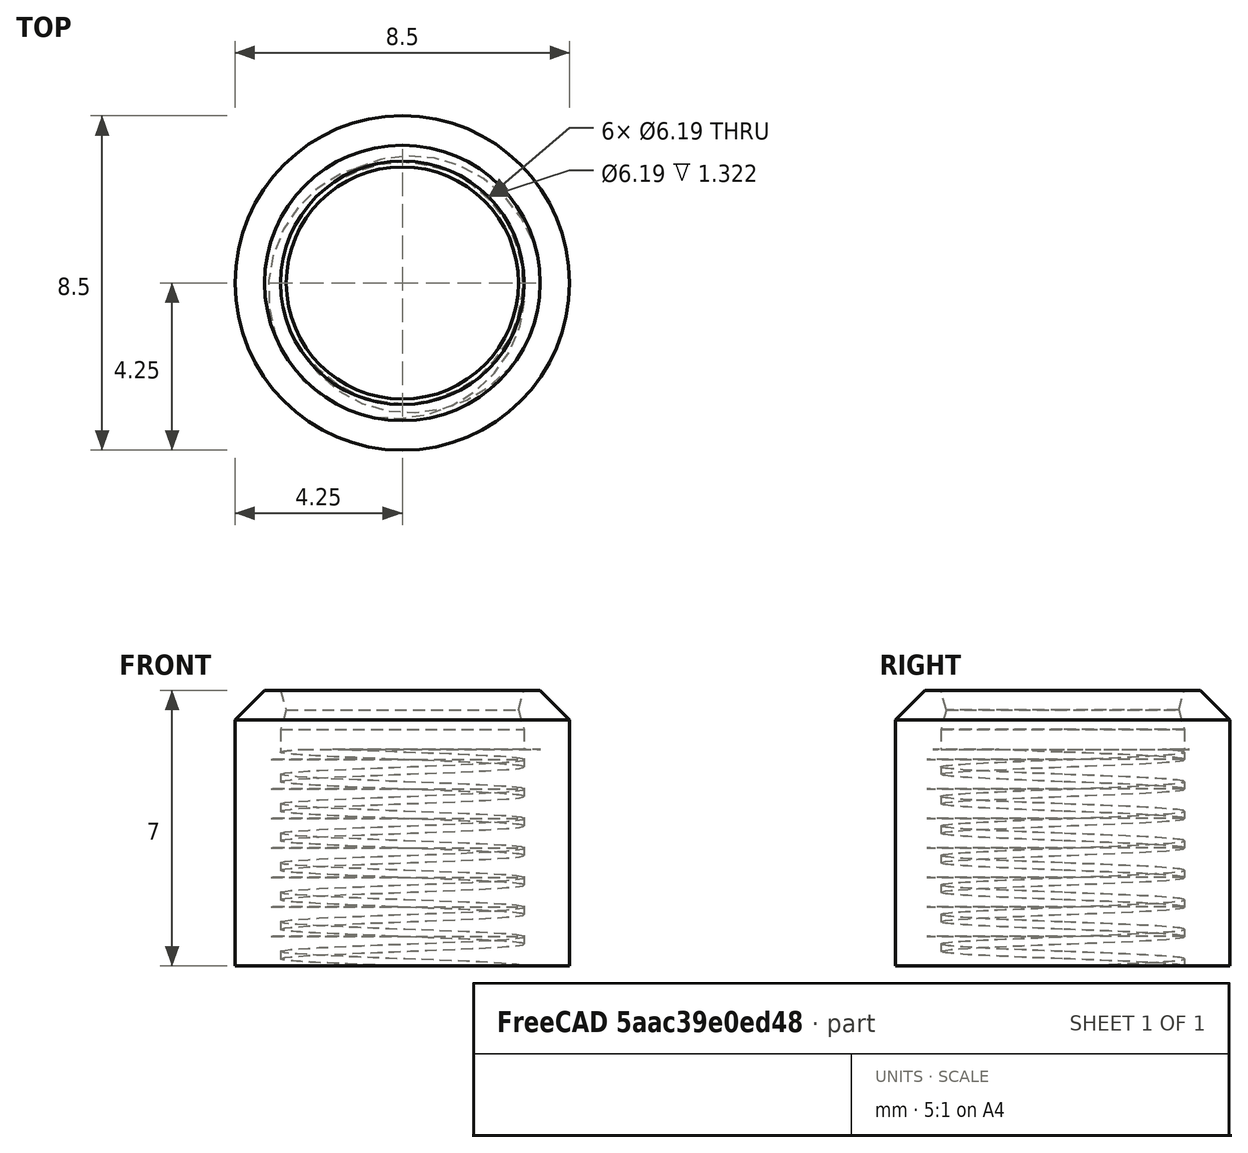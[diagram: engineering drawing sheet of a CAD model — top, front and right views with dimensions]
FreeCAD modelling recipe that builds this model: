
FCSTD DOCUMENT  (FreeCAD 0.21R33668 +26 (Git))
Label: PLASTIC-BUSHING-POT-TEK2
License: All rights reserved
LicenseURL: http://en.wikipedia.org/wiki/All_rights_reserved
objects: TechDraw::DrawViewDimension×9, Sketcher::SketchObject×2, TechDraw::DrawViewBalloon×2, TechDraw::DrawViewAnnotation×2, PartDesign::Revolution×1, TechDraw::DrawSVGTemplate×1, Part::Part2DObjectPython×1, Part::Helix×1, PartDesign::SubtractivePipe×1, PartDesign::Body×1, TechDraw::DrawViewPart×1, TechDraw::DrawComplexSection×1, TechDraw::DrawViewImage×1, TechDraw::DrawPage×1
note: 25 computed .brp shape members not serialized (recipe doc carries the construction recipe); baked Part::Feature solids carry a one-line shape summary decoded from their .brp

FEATURE [Sketcher::SketchObject] Sketch
  FullyConstrained = true
  MapMode = 5
  Placement = pos=(0,0,0) rot=(1,0,0;1.5708rad)
  Support = -> [XZ_Plane]
  sketch-geometry (7):
    g0: LineSegment StartX=-3.095 StartY=6 StartZ=0 EndX=-3.095 EndY=0 EndZ=0
    g1: LineSegment StartX=-3.095 StartY=7 StartZ=0 EndX=-3.5 EndY=7 EndZ=0
    g2: LineSegment StartX=-3.5 StartY=7 StartZ=0 EndX=-4.25 EndY=6.25 EndZ=0
    g3: LineSegment StartX=-4.25 StartY=0 StartZ=0 EndX=-4.25 EndY=6.25 EndZ=0
    g4: LineSegment StartX=-4.25 StartY=0 StartZ=0 EndX=-3.095 EndY=0 EndZ=0
    g5: LineSegment StartX=-3.095 StartY=7 StartZ=0 EndX=-2.95 EndY=6.5 EndZ=0
    g6: LineSegment StartX=-2.95 StartY=6.5 StartZ=0 EndX=-3.095 EndY=6 EndZ=0
  constraints (23):
    c: DistanceY(g6,g1) = 1
    c: Horizontal(g1)
    c: Coincident(g2,g1)
    c: Coincident(g2,g3)
    c: Angle(g2,g1) = 2.35619
    c: DistanceX(g0,g-1) = 3.095
    c: Vertical(g3)
    c: DistanceX(g2,g1) = 0.75
    c: DistanceY(g3,g1) = 7
    c: Vertical(g0)
    c: Coincident(g4,g3)
    c: Horizontal(g4)
    c: Coincident(g4,g0)
    c: PointOnObject(g0,g-1)
    c: DistanceX(g3,g-1) = 4.25
    c: DistanceX(g4,g4) = 1.155
    c: Coincident(g5,g1)
    c: Equal(g6,g5)
    c: Coincident(g6,g5)
    c: DistanceX(g5,g-1) = 2.95
    c: Coincident(g6,g0)
    c: Vertical(g1,g0)
    c: DistanceY(g-1,g5) = 6.5
FEATURE [PartDesign::Revolution] Revolution
  Angle = 360
  Axis = (0,-2e-16,1)
  Base = (0,0,0)
  Placement = pos=(0,0,0) rot=(1,0,0;1.5708rad)
  Profile = -> Sketch
  ReferenceAxis = -> Sketch [V_Axis]
FEATURE [TechDraw::DrawSVGTemplate] Template
  EditableTexts = COLOR=Black,CreationDate=2024/02/16,E.G.APPROVED=APPROVED,FC-Scale=10:1,FC-Title=PLASTIC - BUSHING - POT - TEK2,IntechStudioLtd.=Intech Studio Ltd.,+3 more (map truncated)
  Height = 297
  Orientation = 1
  Template = <userpath>/Documents/grid-hardware/Manufacturing/FreeCAD_technical_drawing_template/A3_LandscapeTD_MODIFIED.svg
  Width = 420
FEATURE [Sketcher::SketchObject] Sketch002
  FullyConstrained = true
  MapMode = 5
  Placement = pos=(0,0,0) rot=(1,0,0;1.5708rad)
  Support = -> [XZ_Plane]
  sketch-geometry (1):
    g0: LineSegment StartX=0 StartY=-1 StartZ=0 EndX=0 EndY=9 EndZ=0
  constraints (4):
    c: PointOnObject(g0,g-2)
    c: PointOnObject(g0,g-2)
    c: DistanceY(g0,g0) = 10
    c: DistanceY(g0,g-1) = 1
FEATURE [Part::Part2DObjectPython] VThreadProfile  # Draft 2D object (typed FeaturePython)
  Area = 33.765
  Closed = true
  Continuity = C2
  Height = 5.5
  Helix = Helix
  Instructions = Expand this with the ... button to view instructions | Sweep this object along a helix of the same pitch to produce your thread. | It is recommended to make the helix in the ThreadProfile workbench. | If there is an active Body the ThreadProfile object will be put into it.,If not it can be dragged and dropped into the body later. | If there is an active Body when the helix is made there will be made a ShapeBinder for it | For internal threads you will need to cut the Sweep object out of a cylinder, or if using Part Design sweep it as a Subtractive Pipe. | Always use Frenet mode | I have provided some presets, but it is possible there could be some errors.  Double check for mission critical applications. | Also, the tolerances might be different from what you wish to have.  I believe the internal minor diameters are all minimum and the external are all maximum.
  InternalOrExternal = 0
  MakeFace = true
  MinorDiameter = 6.188
  Parameterization = 1
  Pitch = 0.75
  Points = (66) [(3.07972,0.296958,0),(3.037,0.591174,0),(2.96624,0.879932,0),(2.86809,1.16056,0),(2.74346,1.43048,0),(2.5935,1.68719,0),(2.41959,1.92832,0),+59 more]
  Presets = 58
  Quality = 11
  ThreadCount = 7.33333
  Variants = 0
  Version = 1.89
  external2S_data = [-0.00461051,-0.00886426,-0.0128148,-0.0165028,-0.0199596,-0.0232105,-0.0262759,-0.0291725,-0.0319145,-0.0345137,-0.0369805,-0.0393235,-0.0415505,-0.0436681,-0.0456823,-0.0475981,-0.0494204,-0.0511532,-0.0528003,-0.0543649,-0.0558502,+698 more]
  external3S_data = [-0.00677828,-0.0128149,-0.0182584,-0.0232106,-0.0277444,-0.0319145,-0.0357632,-0.0393236,-0.0426227,-0.0456823,-0.0485208,-0.0511533,-0.0535928,-0.0558503,-0.0579353,-0.059856,-0.0616195,-0.0632319,-0.0646984,-0.0660239,-0.0672123,+698 more]
  external45_data = [-0.00137363,-0.00271738,-0.00403219,-0.00531893,-0.00657844,-0.00781148,-0.00901878,-0.010201,-0.0113589,-0.012493,-0.0136039,-0.0146921,-0.0157583,-0.0168028,-0.0178261,-0.0188288,-0.0198112,-0.0207738,-0.0217169,-0.0226409,-0.0235462,+698 more]
  external_data = [-0.00235387,-0.00461052,-0.00677828,-0.00886428,-0.0108747,-0.0128149,-0.0146895,-0.0165028,-0.0182584,-0.0199597,-0.0216095,-0.0232106,-0.0247653,-0.0262759,-0.0277444,-0.0291725,-0.0305621,-0.0319145,-0.0332313,-0.0345138,-0.0357632,+698 more]
  internal2S_data = [0,0,0,0,0,0,0,0,0,0,0,0,0,0,0,0,0,0,0,0,0,0,0,0,0,0,0,0,0,0,0,0,0,0,0,0,0,0,0,0,0,0,0,0,0,0,0,0,0,0,0,0,0,0,0,0,0,0,0,0,0,0,0,0,0,0,0,0,0,0,0,0,0,0,0,0,0,0,0,0,0,0,0,0,0,0,0,0,0,0,0.00481128,0.00962256,0.0144338,0.0192451,0.0240564,+624 more]
  internal3S_data = [0,0,0,0,0,0,0,0,0,0,0,0,0,0,0,0,0,0,0,0,0,0,0,0,0,0,0,0,0,0,0,0,0,0,0,0,0,0,0,0,0,0,0,0,0,0,0,0,0,0,0,0,0,0,0,0,0,0,0,0,0.00721688,0.0144338,0.0216506,0.0288675,0.0360844,0.0433013,0.0505181,0.057735,0.0649519,0.0721688,0.0793857,0.0866025,+647 more]
  internal45_data = [0,0,0,0,0,0,0,0,0,0,0,0,0,0,0,0,0,0,0,0,0,0,0,0,0,0,0,0,0,0,0,0,0,0,0,0,0,0,0,0,0,0,0,0,0,0,0,0,0,0,0,0,0,0,0,0,0,0,0,0,0,0,0,0,0,0,0,0,0,0,0,0,0,0,0,0,0,0,0,0,0,0,0,0,0,0,0,0,0,0,0,0,0,0,0,0,0,0,0,0,0,0,0,0,0,0,0,0,0,0,0,0,0,0,0,0,0,0,0,0,+599 more]
  internal_data = [0,0,0,0,0,0,0,0,0,0,0,0,0,0,0,0,0,0,0,0,0,0,0,0,0,0,0,0,0,0,0,0,0,0,0,0,0,0,0,0,0,0,0,0,0,0,0,0,0,0,0,0,0,0,0,0,0,0,0,0,0,0,0,0,0,0,0,0,0,0,0,0,0,0,0,0,0,0,0,0,0,0,0,0,0,0,0,0,0,0,0,0,0,0,0,0,0,0,0,0,0,0,0,0,0,0,0,0,0,0,0,0,0,0,0,0,0,0,0,0,+599 more]
  preset_names = <blob: 3959 chars omitted>
  presets_data = [0,0,0,2.20878,24.1173,24.6888,0.25,0.693,0.729,0.25,0.793,0.829,0.25,0.893,0.929,0.3,1.032,1.075,0.35,1.171,1.221,0.35,1.371,1.421,0.4,1.509,1.567,0.45,1.648,1.713,0.45,1.948,2.013,0.5,2.387,2.459,0.6,2.764,2.85,0.7,3.141,3.242,0.75,3.58,+712 more]
FEATURE [Part::Helix] Helix
  Angle = 0
  AttacherType = Attacher::AttachEngine3D
  Height = 5.5
  LocalCoord = 0
  Pitch = 0.75
  Radius = 1
  SegmentLength = 1
  Style = 0
  expr: AttachmentOffset = VThreadProfile.AttachmentOffset
  expr: Height = VThreadProfile.ThreadCount * VThreadProfile.Pitch
  expr: MapMode = VThreadProfile.MapMode
  expr: MapPathParameter = VThreadProfile.MapPathParameter
  expr: MapReversed = VThreadProfile.MapReversed
  expr: Pitch = VThreadProfile.Pitch
  expr: SegmentLength = 1
  expr: Support = VThreadProfile.Support
FEATURE [PartDesign::SubtractivePipe] SubtractivePipe
  AuxilleryCurvelinear = true
  AuxillerySpineTangent = false
  BaseFeature = -> Revolution
  Binormal = (0,0,0)
  Mode = 2
  Placement = pos=(0,0,0) rot=(1,0,0;1.5708rad)
  Profile = -> VThreadProfile
  Spine = -> Helix [Edge1,Edge2,Edge3,Edge4,Edge5,Edge6,Edge7,Edge8]
  SpineTangent = false
  Transformation = 0
  Transition = 0
FEATURE [PartDesign::Body] Body  label="PLASTIC-BUSHING-POT-TEK2"
  Group = -> [Sketch,Revolution,Sketch002,VThreadProfile,Helix,SubtractivePipe]
  Origin = -> Origin
  Tip = -> SubtractivePipe
FEATURE [TechDraw::DrawViewPart] View
  CoarseView = false
  Direction = (0,-1,0)
  Focus = 100
  HardHidden = false
  IsoCount = 0
  IsoHidden = false
  IsoVisible = true
  LockPosition = false
  Perspective = false
  Rotation = 0
  Scale = 10
  ScaleType = 2
  ScrubCount = 0
  SeamHidden = false
  SeamVisible = true
  SmoothHidden = false
  SmoothVisible = true
  Source = -> [Body]
  X = 105.342
  XDirection = (1,0,1e-06)
  Y = 195.302
FEATURE [TechDraw::DrawComplexSection] ComplexSection  label="Section A - A"
  BaseView = -> View
  CoarseView = false
  CutSurfaceDisplay = 2
  CuttingToolWireObject = -> Sketch002
  Direction = (-1,0,-1e-06)
  FileGeomPattern = C:/Program Files/FreeCAD 0.21/data/Mod/TechDraw/PAT/FCPAT.pat
  FileHatchPattern = C:/Program Files/FreeCAD 0.21/data/Mod/TechDraw/Patterns/simple.svg
  Focus = 100
  FuseBeforeCut = false
  HardHidden = false
  HatchOffset = (0,0,0)
  HatchRotation = 0
  HatchScale = 1
  IsoCount = 0
  IsoHidden = true
  IsoVisible = true
  LockPosition = false
  NameGeomPattern = Gyémánt bevonatú
  Perspective = false
  ProjectionStrategy = 0
  Rotation = -90
  Scale = 10
  ScaleType = 2
  ScrubCount = 0
  SeamHidden = false
  SeamVisible = true
  SectionDirection = 4
  SectionNormal = (-1,0,-1e-06)
  SectionOrigin = (0,0,0)
  SectionSymbol = A
  SmoothHidden = false
  SmoothVisible = true
  Source = -> [Body]
  TrimAfterCut = false
  X = 278.137
  XDirection = (1e-06,0,-1)
  Y = 193.227
FEATURE [TechDraw::DrawViewDimension] Dimension
  AngleOverride = false
  Arbitrary = false
  ArbitraryTolerances = false
  EqualTolerance = true
  ExtensionAngle = 0
  FormatSpec = %.2w
  FormatSpecOverTolerance = %+.2w
  FormatSpecUnderTolerance = %+.2w
  Inverted = false
  LineAngle = 0
  LockPosition = false
  MeasureType = 1
  OverTolerance = 0
  References2D = -> [View]
  Rotation = 0
  ScaleType = 0
  TheoreticalExact = false
  Type = 2
  UnderTolerance = 0
  X = -79.9347
  Y = -3.56941
FEATURE [TechDraw::DrawViewDimension] Dimension006
  AngleOverride = false
  Arbitrary = false
  ArbitraryTolerances = false
  EqualTolerance = true
  ExtensionAngle = 0
  FormatSpec = ⌀%.2w
  FormatSpecOverTolerance = %+.2w
  FormatSpecUnderTolerance = %+.2w
  Inverted = false
  LineAngle = 0
  LockPosition = false
  MeasureType = 1
  OverTolerance = 0
  References2D = -> [View]
  Rotation = 0
  ScaleType = 0
  TheoreticalExact = false
  Type = 0
  UnderTolerance = 0
  X = -1.09206
  Y = -55.2451
FEATURE [TechDraw::DrawViewDimension] Dimension007
  AngleOverride = false
  Arbitrary = false
  ArbitraryTolerances = false
  EqualTolerance = true
  ExtensionAngle = 0
  FormatSpec = %.2w×45°
  FormatSpecOverTolerance = %+.2w
  FormatSpecUnderTolerance = %+.2w
  Inverted = false
  LineAngle = 0
  LockPosition = false
  MeasureType = 1
  OverTolerance = 0
  References2D = -> [ComplexSection]
  Rotation = 0
  ScaleType = 0
  TheoreticalExact = false
  Type = 2
  UnderTolerance = 0
  X = 63.4815
  Y = 51.4567
FEATURE [TechDraw::DrawViewDimension] Dimension014
  AngleOverride = false
  Arbitrary = false
  ArbitraryTolerances = false
  EqualTolerance = true
  ExtensionAngle = 0
  FormatSpec = %.2w
  FormatSpecOverTolerance = %+.2w
  FormatSpecUnderTolerance = %+.2w
  Inverted = false
  LineAngle = 0
  LockPosition = false
  MeasureType = 1
  OverTolerance = 0
  References2D = -> [View]
  Rotation = 0
  ScaleType = 0
  TheoreticalExact = false
  Type = 2
  UnderTolerance = 0
  X = 57.5401
  Y = -3.22906
FEATURE [TechDraw::DrawViewBalloon] Balloon
  BubbleShape = 1
  EndType = 0
  EndTypeScale = 1
  KinkLength = 23
  LockPosition = false
  OriginX = -3.35
  OriginY = -2.91733
  Rotation = 0
  ScaleType = 0
  ShapeScale = 1
  SourceView = -> ComplexSection
  TextWrapLen = -1
  X = -8.78664
  Y = -7.08142
FEATURE [TechDraw::DrawViewAnnotation] Annotation
  Font = osifont
  LineSpace = 100
  LockPosition = false
  MaxWidth = -1
  Rotation = 0
  ScaleType = 0
  Text = M7x0,75
  TextSize = 4
  TextStyle = 0
  X = 204.281
  Y = 126.418
FEATURE [TechDraw::DrawViewAnnotation] Annotation001
  Font = osifont
  LineSpace = 100
  LockPosition = false
  MaxWidth = -1
  Rotation = 0
  ScaleType = 0
  Text = Section A-A
  TextSize = 4
  TextStyle = 0
  X = 279.191
  Y = 142.827
FEATURE [TechDraw::DrawViewDimension] Dimension022
  AngleOverride = false
  Arbitrary = false
  ArbitraryTolerances = false
  EqualTolerance = true
  ExtensionAngle = 0
  FormatSpec = ⌀%.2w
  FormatSpecOverTolerance = %+.2w
  FormatSpecUnderTolerance = %+.2w
  Inverted = false
  LineAngle = 0
  LockPosition = false
  MeasureType = 1
  OverTolerance = 0
  References2D = -> [ComplexSection]
  Rotation = 0
  ScaleType = 0
  TheoreticalExact = false
  Type = 1
  UnderTolerance = 0
  X = -0.136376
  Y = 59.7496
FEATURE [TechDraw::DrawViewDimension] Dimension023
  AngleOverride = false
  Arbitrary = false
  ArbitraryTolerances = false
  EqualTolerance = true
  ExtensionAngle = 0
  FormatSpec = ⌀%.2w
  FormatSpecOverTolerance = %+.2w
  FormatSpecUnderTolerance = %+.2w
  Inverted = false
  LineAngle = 0
  LockPosition = false
  MeasureType = 1
  OverTolerance = 0
  References2D = -> [ComplexSection]
  Rotation = 0
  ScaleType = 0
  TheoreticalExact = false
  Type = 1
  UnderTolerance = 0
  X = -0.05614
  Y = 47.3861
FEATURE [TechDraw::DrawViewImage] ActiveView001
  Height = 100
  ImageFile = <userpath>/AppData/Local/Temp/FreeCAD/Cache/FreeCAD_Doc_08b8b2a3-d6cd-4e8a-b76b-68cd6ee703e2_b0381e_12992/Pag507.tmp.png
  LockPosition = false
  Rotation = 0
  ScaleType = 2
  Width = 100
  X = 103.324
  Y = 60.3096
FEATURE [TechDraw::DrawViewDimension] Dimension024
  AngleOverride = false
  Arbitrary = false
  ArbitraryTolerances = false
  EqualTolerance = true
  ExtensionAngle = 0
  FormatSpec = %.2w
  FormatSpecOverTolerance = %+.2w
  FormatSpecUnderTolerance = %+.2w
  Inverted = false
  LineAngle = 0
  LockPosition = false
  MeasureType = 1
  OverTolerance = 0
  References2D = -> [ComplexSection]
  Rotation = 0
  ScaleType = 0
  TheoreticalExact = false
  Type = 2
  UnderTolerance = 0
  X = -58.3373
  Y = 31.8528
FEATURE [TechDraw::DrawViewDimension] Dimension025
  AngleOverride = false
  Arbitrary = false
  ArbitraryTolerances = false
  EqualTolerance = true
  ExtensionAngle = 0
  FormatSpec = (%.2w)
  FormatSpecOverTolerance = %+.2w
  FormatSpecUnderTolerance = %+.2w
  Inverted = false
  LineAngle = 0
  LockPosition = false
  MeasureType = 1
  OverTolerance = 0
  References2D = -> [ComplexSection]
  Rotation = 0
  ScaleType = 0
  TheoreticalExact = false
  Type = 2
  UnderTolerance = 0
  X = 57.4856
  Y = -2.99998
FEATURE [TechDraw::DrawViewDimension] Dimension026
  AngleOverride = false
  Arbitrary = false
  ArbitraryTolerances = false
  EqualTolerance = true
  ExtensionAngle = 0
  FormatSpec = %.2w
  FormatSpecOverTolerance = %+.2w
  FormatSpecUnderTolerance = %+.2w
  Inverted = false
  LineAngle = 0
  LockPosition = false
  MeasureType = 1
  OverTolerance = 0
  References2D = -> [ComplexSection]
  Rotation = 0
  ScaleType = 0
  TheoreticalExact = false
  Type = 2
  UnderTolerance = 0
  X = -58.6862
  Y = -4.57985
FEATURE [TechDraw::DrawViewBalloon] Balloon001
  BubbleShape = 2
  EndType = 6
  EndTypeScale = 1
  KinkLength = 0
  LockPosition = false
  OriginX = -64.0153
  OriginY = -11.7113
  Rotation = 0
  ScaleType = 0
  ShapeScale = 1
  SourceView = -> Dimension026
  Text = 2
  TextWrapLen = -1
  X = -65.068
  Y = -15.0747
FEATURE [TechDraw::DrawPage] Page001  label="PLASTIC-BUSHING-POT-TEK2_Drawing"
  KeepUpdated = true
  NextBalloonIndex = 4
  ProjectionType = 0
  Template = -> Template
  Views = -> [View,ComplexSection,Dimension,Dimension006,Dimension007,Dimension014,Balloon,Annotation,Annotation001,Dimension022,Dimension023,ActiveView001,Dimension024,Dimension025,Dimension026,Balloon001]
